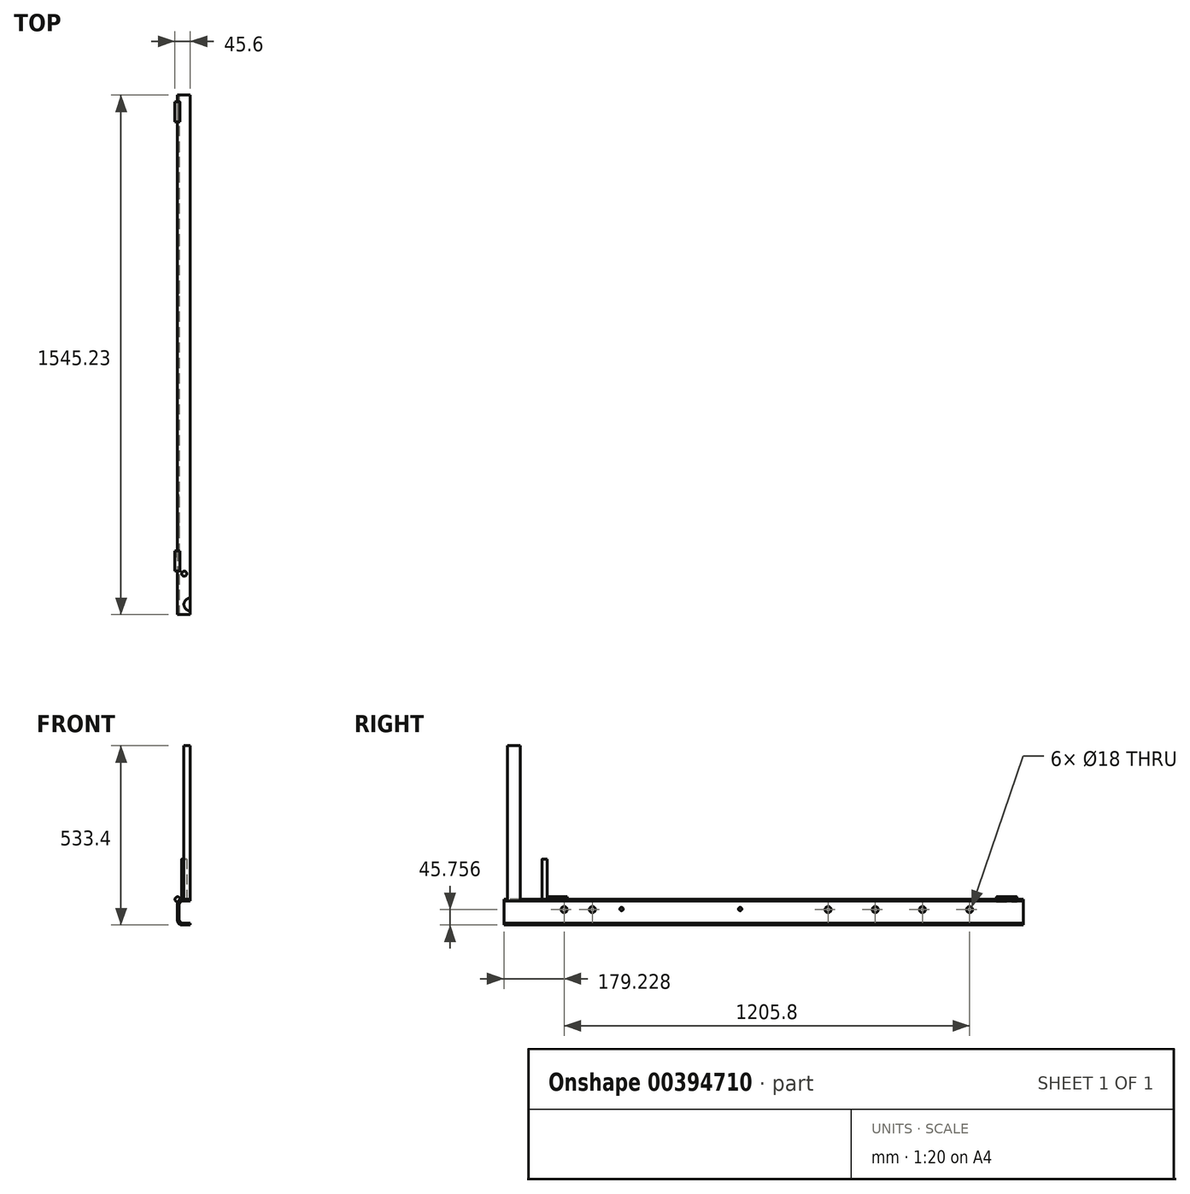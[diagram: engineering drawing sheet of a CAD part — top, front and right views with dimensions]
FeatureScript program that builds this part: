
annotation { "Feature Type Name" : "Feature", "Feature Type Description" : "" }
export const myFeature = defineFeature(function(context is Context, id is Id, definition is map)
    precondition{}
    {
        {
            var Q0;
            Q0=qCreatedBy(makeId("Front.planeOp"),FACE);
            var sketch = newSketch(context, id + "F0", { "sketchPlane" : qUnion([Q0])});
            skLineSegment(sketch, "E0.bottom", {"start": v(12.7, 0) * mm, "end": v(63.5, 0) * mm});
            skLineSegment(sketch, "E0.top", {"start": v(12.7, 76.2) * mm, "end": v(63.5, 76.2) * mm});
            skLineSegment(sketch, "E0.left", {"start": v(0, 12.7) * mm, "end": v(0, 63.5) * mm});
            skLineSegment(sketch, "E0.right", {"start": v(76.2, 12.7) * mm, "end": v(76.2, 63.5) * mm});
            skPoint(sketch, "E1.visualSharp", {"position": v(0, 76.2) * mm});
            skArc(sketch, "E1.filletArc", {"start": v(12.7, 76.2) * mm, "mid": v(3.72, 72.48) * mm, "end": v(0, 63.5) * mm});
            skPoint(sketch, "E2.visualSharp", {"position": v(76.2, 76.2) * mm});
            skArc(sketch, "E2.filletArc", {"start": v(76.2, 63.5) * mm, "mid": v(72.48, 72.48) * mm, "end": v(63.5, 76.2) * mm});
            skPoint(sketch, "E3.visualSharp", {"position": v(0, 0) * mm});
            skArc(sketch, "E3.filletArc", {"start": v(0, 12.7) * mm, "mid": v(3.72, 3.72) * mm, "end": v(12.7, 0) * mm});
            skPoint(sketch, "E4.visualSharp", {"position": v(76.2, 0) * mm});
            skArc(sketch, "E4.filletArc", {"start": v(63.5, 0) * mm, "mid": v(72.48, 3.72) * mm, "end": v(76.2, 12.7) * mm});
            skSolve(sketch);
        }
        {
            var Q0;
            Q0=qSketchRegion(id+"F0",true);
            extrude(context, id + "F1", {"entities" : qUnion([Q0]), "oppositeDirection" : true, "depth" : 1525.23 * mm});
        }
        {
            var Q0;
            Q0=makeQuery(id+"F1.opExtrude","CAP_FACE",FACE,{"disambiguationData":[OSD([sQuery(id+"F0.wireOp",EDGE,"E0.bottom"),sQuery(id+"F0.wireOp",EDGE,"E0.top"),sQuery(id+"F0.wireOp",EDGE,"E0.left"),sQuery(id+"F0.wireOp",EDGE,"E0.right"),sQuery(id+"F0.wireOp",EDGE,"E1.filletArc"),sQuery(id+"F0.wireOp",EDGE,"E2.filletArc"),sQuery(id+"F0.wireOp",EDGE,"E3.filletArc"),sQuery(id+"F0.wireOp",EDGE,"E4.filletArc")])],"isStart":true});
            var sketch = newSketch(context, id + "F2", { "sketchPlane" : qUnion([Q0])});
            skLineSegment(sketch, "E5", {"start": v(0, 38.1) * mm, "end": v(4.76, 38.1) * mm, "construction": true});
            skLineSegment(sketch, "E6", {"start": v(76.2, 38.1) * mm, "end": v(71.44, 38.1) * mm, "construction": true});
            skPoint(sketch, "E6.endSnap0", {"position": v(76.2, 38.1) * mm});
            skLineSegment(sketch, "E7", {"start": v(38.1, 76.2) * mm, "end": v(38.1, 71.44) * mm, "construction": true});
            skLineSegment(sketch, "E8", {"start": v(38.1, 0) * mm, "end": v(38.1, 4.76) * mm, "construction": true});
            skLineSegment(sketch, "E9", {"start": v(38.1, 4.76) * mm, "end": v(17.46, 4.76) * mm});
            skLineSegment(sketch, "E10", {"start": v(4.76, 17.46) * mm, "end": v(4.76, 58.74) * mm});
            skLineSegment(sketch, "E11", {"start": v(17.46, 71.44) * mm, "end": v(58.74, 71.44) * mm});
            skLineSegment(sketch, "E12", {"start": v(71.44, 58.74) * mm, "end": v(71.44, 17.46) * mm});
            skLineSegment(sketch, "E13", {"start": v(58.74, 4.76) * mm, "end": v(38.1, 4.76) * mm});
            skPoint(sketch, "E14.visualSharp", {"position": v(4.76, 71.44) * mm});
            skArc(sketch, "E14.filletArc", {"start": v(17.46, 71.44) * mm, "mid": v(8.48, 67.72) * mm, "end": v(4.76, 58.74) * mm});
            skPoint(sketch, "E15.visualSharp", {"position": v(71.44, 71.44) * mm});
            skArc(sketch, "E15.filletArc", {"start": v(71.44, 58.74) * mm, "mid": v(67.72, 67.72) * mm, "end": v(58.74, 71.44) * mm});
            skPoint(sketch, "E16.visualSharp", {"position": v(71.44, 4.76) * mm});
            skArc(sketch, "E16.filletArc", {"start": v(58.74, 4.76) * mm, "mid": v(67.72, 8.48) * mm, "end": v(71.44, 17.46) * mm});
            skPoint(sketch, "E17.visualSharp", {"position": v(4.76, 4.76) * mm});
            skArc(sketch, "E17.filletArc", {"start": v(4.76, 17.46) * mm, "mid": v(8.48, 8.48) * mm, "end": v(17.46, 4.76) * mm});
            skSolve(sketch);
        }
        {
            var Q0;
            Q0=makeQuery(id+"F2.imprint","IMPRINT",FACE,{"disambiguationData":[TD([[makeQuery(id+"F2.imprint","IMPRINT",EDGE,{"derivedFrom":sQuery(id+"F2.wireOp",EDGE,"E9")}),-1.0]])]});
            extrude(context, id + "F3", {"entities" : qUnion([Q0]), "operationType" : NewBodyOperationType.REMOVE, "oppositeDirection" : true, "depth" : 1525.23 * mm});
        }
        {
            var Q0;
            Q0=makeQuery(id+"F1.opExtrude","SWEPT_FACE",FACE,{"disambiguationData":[OSD([sQuery(id+"F0.wireOp",EDGE,"E0.right")])]});
            var sketch = newSketch(context, id + "F4", { "sketchPlane" : qUnion([Q0])});
            skLineSegment(sketch, "E18", {"start": v(1525.23, 63.5) * mm, "end": v(1525.23, 76.2) * mm, "construction": true});
            skLineSegment(sketch, "E19", {"start": v(1525.23, 76.2) * mm, "end": v(1525.23, 46.2) * mm, "construction": true});
            skLineSegment(sketch, "E20", {"start": v(1525.23, 46.2) * mm, "end": v(1335.23, 46.2) * mm, "construction": true});
            skLineSegment(sketch, "E21", {"start": v(1335.23, 46.2) * mm, "end": v(1105.03, 46.2) * mm, "construction": true});
            skLineSegment(sketch, "E22", {"start": v(1105.03, 46.2) * mm, "end": v(653.53, 46.2) * mm, "construction": true});
            skLineSegment(sketch, "E23", {"start": v(653.53, 46.2) * mm, "end": v(381.53, 46.2) * mm, "construction": true});
            skLineSegment(sketch, "E24", {"start": v(381.53, 46.2) * mm, "end": v(179.53, 46.2) * mm, "construction": true});
            skSolve(sketch);
        }
        {
            var Q0;
            Q0=sQuery(id+"F4.wireOp",VERTEX,"E21.start");
            var Q1;
            Q1=sQuery(id+"F4.wireOp",VERTEX,"E21.end");
            var Q2;
            Q2=sQuery(id+"F4.wireOp",VERTEX,"E23.start");
            var Q3;
            Q3=sQuery(id+"F4.wireOp",VERTEX,"E24.start");
            var Q4;
            Q4=sQuery(id+"F4.wireOp",VERTEX,"15NCYrLK-5f7F-d4hg-Meu1-zmrvhpbFYJVG.start");
            var Q5;
            Q5=sQuery(id+"F4.wireOp",VERTEX,"E24.end");
            var Q6;
            Q6=makeQuery(id+"F1.opExtrude","SWEPT_BODY",BODY,{"disambiguationData":[OSD([sQuery(id+"F0.wireOp",EDGE,"E0.bottom"),sQuery(id+"F0.wireOp",EDGE,"E0.top"),sQuery(id+"F0.wireOp",EDGE,"E0.left"),sQuery(id+"F0.wireOp",EDGE,"E0.right"),sQuery(id+"F0.wireOp",EDGE,"E1.filletArc"),sQuery(id+"F0.wireOp",EDGE,"E2.filletArc"),sQuery(id+"F0.wireOp",EDGE,"E3.filletArc"),sQuery(id+"F0.wireOp",EDGE,"E4.filletArc")])]});
            hole(context, id + "F5", {"style" : HoleStyle.SIMPLE, "endStyle" : HoleEndStyle.BLIND, "holeDiameter" : 19 * mm, "holeDepth" : 5 * mm, "isTappedThrough" : true, "tappedDepth" : 12 * mm, "tapClearance" : 3, "locations" : qUnion([Q0, Q1, Q2, Q3, Q4, Q5]), "scope" : qUnion([Q6])});
        }
        {
            var Q0;
            Q0=makeQuery(id+"F1.opExtrude","SWEPT_FACE",FACE,{"disambiguationData":[OSD([sQuery(id+"F0.wireOp",EDGE,"E0.right")])]});
            var sketch = newSketch(context, id + "F6", { "sketchPlane" : qUnion([Q0])});
            skLineSegment(sketch, "E25", {"start": v(1525.23, 63.5) * mm, "end": v(1525.23, 76.2) * mm});
            skLineSegment(sketch, "E26", {"start": v(1525.23, 76.2) * mm, "end": v(1525.23, 31.2) * mm, "construction": true});
            skLineSegment(sketch, "E27", {"start": v(1525.23, 31.2) * mm, "end": v(1442.06, 31.2) * mm, "construction": true});
            skLineSegment(sketch, "E28", {"start": v(1442.06, 31.2) * mm, "end": v(1218.7, 31.2) * mm, "construction": true});
            skLineSegment(sketch, "E29", {"start": v(1218.7, 31.2) * mm, "end": v(979.53, 31.2) * mm, "construction": true});
            skLineSegment(sketch, "E30", {"start": v(979.53, 31.2) * mm, "end": v(760.33, 31.2) * mm, "construction": true});
            skLineSegment(sketch, "E31", {"start": v(760.33, 31.2) * mm, "end": v(501.13, 31.2) * mm, "construction": true});
            skLineSegment(sketch, "E32", {"start": v(501.13, 31.2) * mm, "end": v(261.93, 31.2) * mm, "construction": true});
            skSolve(sketch);
        }
        {
            var Q0;
            Q0=sQuery(id+"F6.wireOp",VERTEX,"E32.end");
            var Q1;
            Q1=sQuery(id+"F6.wireOp",VERTEX,"E32.start");
            var Q2;
            Q2=sQuery(id+"F6.wireOp",VERTEX,"E31.start");
            var Q3;
            Q3=sQuery(id+"F6.wireOp",VERTEX,"E30.start");
            var Q4;
            Q4=sQuery(id+"F6.wireOp",VERTEX,"E28.end");
            var Q5;
            Q5=makeQuery(id+"F1.opExtrude","SWEPT_BODY",BODY,{"disambiguationData":[OSD([sQuery(id+"F0.wireOp",EDGE,"E0.bottom"),sQuery(id+"F0.wireOp",EDGE,"E0.top"),sQuery(id+"F0.wireOp",EDGE,"E0.left"),sQuery(id+"F0.wireOp",EDGE,"E0.right"),sQuery(id+"F0.wireOp",EDGE,"E1.filletArc"),sQuery(id+"F0.wireOp",EDGE,"E2.filletArc"),sQuery(id+"F0.wireOp",EDGE,"E3.filletArc"),sQuery(id+"F0.wireOp",EDGE,"E4.filletArc")])]});
            hole(context, id + "F7", {"style" : HoleStyle.SIMPLE, "endStyle" : HoleEndStyle.BLIND, "holeDiameter" : 9 * mm, "holeDepth" : 5 * mm, "isTappedThrough" : true, "tappedDepth" : 12 * mm, "tapClearance" : 3, "locations" : qUnion([Q0, Q1, Q2, Q3, Q4]), "scope" : qUnion([Q5])});
        }
        {
            var Q0;
            Q0=makeQuery(id+"F1.opExtrude","SWEPT_FACE",FACE,{"disambiguationData":[OSD([sQuery(id+"F0.wireOp",EDGE,"E0.top")])]});
            var sketch = newSketch(context, id + "F8", { "sketchPlane" : qUnion([Q0])});
            skLineSegment(sketch, "E33", {"start": v(38.1, 0) * mm, "end": v(38.1, 30) * mm, "construction": true});
            skCircle(sketch, "E34", {"center": v(38.1, 30) * mm, "radius": 19.05 * mm});
            skSolve(sketch);
        }
        {
            var Q0;
            Q0=makeQuery(id+"F8.imprint","IMPRINT",FACE,{"disambiguationData":[TD([[makeQuery(id+"F8.imprint","IMPRINT",EDGE,{"derivedFrom":sQuery(id+"F8.wireOp",EDGE,"E34")}),1.0]])]});
            extrude(context, id + "F9", {"entities" : qUnion([Q0]), "operationType" : NewBodyOperationType.ADD, "depth" : 457.2 * mm});
        }
        {
            var Q0;
            {var subQ0=sQuery(id+"F0.wireOp",EDGE,"E0.top");Q0=makeQuery(id+"FTddWvQlXHfw4Uw_1.boolean.opBoolean","MERGE",FACE,{"derivedFrom":[makeQuery(id+"F1.opExtrude","SWEPT_FACE",FACE,{"disambiguationData":[OSD([subQ0])]}),makeQuery(id+"FTddWvQlXHfw4Uw_1.opExtrude","SWEPT_FACE",FACE,{"disambiguationData":[OSD([subQ0])]})]});}
            var sketch = newSketch(context, id + "F10", { "sketchPlane" : qUnion([Q0])});
            skLineSegment(sketch, "E35", {"start": v(12.7, 0) * mm, "end": v(12.7, 30) * mm, "construction": true});
            skLineSegment(sketch, "E36", {"start": v(12.7, 30) * mm, "end": v(12.7, 49.05) * mm, "construction": true});
            skLineSegment(sketch, "E37", {"start": v(12.7, 49.05) * mm, "end": v(12.7, 121.55) * mm, "construction": true});
            skLineSegment(sketch, "E38", {"start": v(12.7, 121.55) * mm, "end": v(20.2, 121.55) * mm, "construction": true});
            skCircle(sketch, "E39", {"center": v(20.2, 121.55) * mm, "radius": 7.5 * mm});
            skSolve(sketch);
        }
        {
            var Q0;
            Q0=makeQuery(id+"F10.imprint","IMPRINT",FACE,{"disambiguationData":[TD([[makeQuery(id+"F10.imprint","IMPRINT",EDGE,{"derivedFrom":sQuery(id+"F10.wireOp",EDGE,"E39")}),1.0]])]});
            extrude(context, id + "F11", {"entities" : qUnion([Q0]), "operationType" : NewBodyOperationType.ADD, "depth" : 120 * mm});
        }
        {
            var Q0;
            Q0=makeQuery(id+"F1.opExtrude","CAP_FACE",FACE,{"disambiguationData":[OSD([sQuery(id+"F0.wireOp",EDGE,"E0.bottom"),sQuery(id+"F0.wireOp",EDGE,"E0.top"),sQuery(id+"F0.wireOp",EDGE,"E0.left"),sQuery(id+"F0.wireOp",EDGE,"E0.right"),sQuery(id+"F0.wireOp",EDGE,"E1.filletArc"),sQuery(id+"F0.wireOp",EDGE,"E2.filletArc"),sQuery(id+"F0.wireOp",EDGE,"E3.filletArc"),sQuery(id+"F0.wireOp",EDGE,"E4.filletArc")])],"isStart":false});
            extrude(context, id + "F12", {"entities" : qUnion([Q0]), "operationType" : NewBodyOperationType.ADD, "depth" : 20 * mm});
        }
        {
            var Q0;
            {var subQ0=sQuery(id+"F0.wireOp",EDGE,"E0.top");Q0=makeQuery(id+"F12.boolean.opBoolean","MERGE",FACE,{"derivedFrom":[makeQuery(id+"F1.opExtrude","SWEPT_FACE",FACE,{"disambiguationData":[OSD([subQ0])]}),makeQuery(id+"F12.opExtrude","SWEPT_FACE",FACE,{"disambiguationData":[OSD([subQ0])]})]});}
            var sketch = newSketch(context, id + "F13", { "sketchPlane" : qUnion([Q0])});
            skLineSegment(sketch, "E40", {"start": v(12.7, 121.55) * mm, "end": v(20.2, 121.55) * mm, "construction": true});
            skLineSegment(sketch, "E41", {"start": v(20.2, 121.55) * mm, "end": v(20.2, 129.05) * mm, "construction": true});
            skLineSegment(sketch, "E42", {"start": v(20.2, 129.05) * mm, "end": v(55.2, 129.05) * mm, "construction": true});
            skLineSegment(sketch, "E43", {"start": v(55.2, 129.05) * mm, "end": v(55.2, 0) * mm, "construction": true});
            skSolve(sketch);
        }
        {
            var Q0;
            {var subQ0=sQuery(id+"F0.wireOp",EDGE,"E0.right");Q0=makeQuery(id+"F12.boolean.opBoolean","MERGE",FACE,{"derivedFrom":[makeQuery(id+"F1.opExtrude","SWEPT_FACE",FACE,{"disambiguationData":[OSD([subQ0])]}),makeQuery(id+"F12.opExtrude","SWEPT_FACE",FACE,{"disambiguationData":[OSD([subQ0])]})]});}
            var sketch = newSketch(context, id + "F14", { "sketchPlane" : qUnion([Q0])});
            skLineSegment(sketch, "E44", {"start": v(0, 63.5) * mm, "end": v(129.05, 63.5) * mm, "construction": true});
            skSolve(sketch);
        }
        {
            var Q0;
            Q0=sQuery(id+"F13.wireOp",VERTEX,"E41.end");
            var Q1;
            Q1=sQuery(id+"F13.wireOp",VERTEX,"E42.end");
            var Q2;
            Q2=sQuery(id+"F14.wireOp",VERTEX,"E44.end");
            cPlane(context, id + "F15", {"entities" : qUnion([Q0, Q1, Q2]), "cplaneType" : CPlaneType.THREE_POINT, "offset" : 25 * mm, "width" : 150 * mm, "height" : 150 * mm});
        }
        {
            var Q0;
            Q0=qCreatedBy(id+"F15.planeOp",FACE);
            var sketch = newSketch(context, id + "F16", { "sketchPlane" : qUnion([Q0])});
            skLineSegment(sketch, "E45", {"start": v(0, 0) * mm, "end": v(0, 76.2) * mm, "construction": true});
            skCircle(sketch, "E46", {"center": v(0, 76.2) * mm, "radius": 7.5 * mm});
            skSolve(sketch);
        }
        {
            var Q0;
            Q0=qSketchRegion(id+"F16",true);
            extrude(context, id + "F17", {"entities" : qUnion([Q0]), "operationType" : NewBodyOperationType.ADD, "oppositeDirection" : true, "depth" : 60 * mm});
        }
        {
            var Q0;
            {var subQ6=sQuery(id+"F0.wireOp",EDGE,"E0.top");Q0=makeQuery(id+"F13.imprint","IMPRINT",FACE,{"disambiguationData":[TD([[makeQuery(id+"F13.imprint","IMPRINT",EDGE,{"derivedFrom":makeQuery(id+"F1.opExtrude","CAP_EDGE",EDGE,{"disambiguationData":[OSD([subQ6])],"isStart":true})}),1.0]])]});}
            var sketch = newSketch(context, id + "F18", { "sketchPlane" : qUnion([Q0])});
            skLineSegment(sketch, "E47", {"start": v(0, 0) * mm, "end": v(38.1, 0) * mm, "construction": true});
            skLineSegment(sketch, "E48", {"start": v(38.1, 0) * mm, "end": v(38.1, 1545.43) * mm, "construction": true});
            skSolve(sketch);
        }
        {
            var Q0;
            {var subQ6=sQuery(id+"F0.wireOp",EDGE,"E0.top");Q0=makeQuery(id+"F13.imprint","IMPRINT",FACE,{"disambiguationData":[TD([[makeQuery(id+"F13.imprint","IMPRINT",EDGE,{"derivedFrom":makeQuery(id+"F1.opExtrude","CAP_EDGE",EDGE,{"disambiguationData":[OSD([subQ6])],"isStart":true})}),1.0]])]});}
            var sketch = newSketch(context, id + "F19", { "sketchPlane" : qUnion([Q0])});
            skLineSegment(sketch, "E49", {"start": v(0, 0) * mm, "end": v(0, 1525.23) * mm, "construction": true});
            skLineSegment(sketch, "E50", {"start": v(0, 1525.23) * mm, "end": v(75.73, 1525.23) * mm, "construction": true});
            skSolve(sketch);
        }
        {
            var Q0;
            {var subQ0=sQuery(id+"F0.wireOp",EDGE,"E0.right");Q0=makeQuery(id+"F14.imprint","IMPRINT",FACE,{"disambiguationData":[TD([[makeQuery(id+"F14.imprint","IMPRINT",EDGE,{"derivedFrom":makeQuery(id+"F1.opExtrude","CAP_EDGE",EDGE,{"disambiguationData":[OSD([subQ0])],"isStart":true})}),-1.0]])]});}
            var sketch = newSketch(context, id + "F20", { "sketchPlane" : qUnion([Q0])});
            skLineSegment(sketch, "E51", {"start": v(0, 33.48) * mm, "end": v(1525.23, 33.48) * mm, "construction": true});
            skSolve(sketch);
        }
        {
            var Q0;
            Q0=sQuery(id+"F20.wireOp",VERTEX,"E51.end");
            var Q1;
            Q1=sQuery(id+"F19.wireOp",VERTEX,"E50.end");
            var Q2;
            Q2=sQuery(id+"F19.wireOp",VERTEX,"E49.end");
            cPlane(context, id + "F21", {"entities" : qUnion([Q0, Q1, Q2]), "cplaneType" : CPlaneType.THREE_POINT, "offset" : 25 * mm, "width" : 150 * mm, "height" : 150 * mm});
        }
        {
            var Q0;
            Q0=qCreatedBy(id+"F21.planeOp",FACE);
            var sketch = newSketch(context, id + "F22", { "sketchPlane" : qUnion([Q0])});
            skLineSegment(sketch, "E52", {"start": v(0, 0) * mm, "end": v(0, 76.2) * mm, "construction": true});
            skCircle(sketch, "E53", {"center": v(0, 76.2) * mm, "radius": 7.5 * mm});
            skSolve(sketch);
        }
        {
            var Q0;
            Q0=makeQuery(id+"F22.imprint","IMPRINT",FACE,{"disambiguationData":[TD([[makeQuery(id+"F22.imprint","IMPRINT",EDGE,{"derivedFrom":sQuery(id+"F22.wireOp",EDGE,"E53")}),1.0]])]});
            extrude(context, id + "F23", {"entities" : qUnion([Q0]), "operationType" : NewBodyOperationType.ADD, "oppositeDirection" : true, "depth" : 60 * mm});
        }
        {
            var Q0;
            Q0=makeQuery(id+"F12.opExtrude","CAP_EDGE",EDGE,{"disambiguationData":[OSD([sQuery(id+"F0.wireOp",EDGE,"E0.top")])],"isStart":false});
            cPoint(context, id + "F24", {"entities" : qUnion([Q0]), "parameter" : 0.5});
        }
        {
            var Q0;
            Q0=sQuery(id+"F18.wireOp",EDGE,"E48");
            cPoint(context, id + "F25", {"entities" : qUnion([Q0]), "parameter" : 0.5});
        }
        {
            var Q0;
            Q0=makeQuery(id+"F12.opExtrude","CAP_EDGE",EDGE,{"disambiguationData":[OSD([sQuery(id+"F0.wireOp",EDGE,"E0.bottom")])],"isStart":false});
            cPoint(context, id + "F26", {"entities" : qUnion([Q0]), "parameter" : 0.5});
        }
        {
            var Q0;
            Q0=qCreatedBy(id+"F24",VERTEX);
            var Q1;
            Q1=qCreatedBy(id+"F25",VERTEX);
            var Q2;
            Q2=qCreatedBy(id+"F26",VERTEX);
            cPlane(context, id + "F27", {"entities" : qUnion([Q0, Q1, Q2]), "cplaneType" : CPlaneType.THREE_POINT, "offset" : 25 * mm, "width" : 150 * mm, "height" : 150 * mm});
        }
        {
            var Q0;
            Q0=sQuery(id+"F6.wireOp",VERTEX,"E28.start");
            var Q1;
            Q1=makeQuery(id+"F1.opExtrude","SWEPT_BODY",BODY,{"disambiguationData":[OSD([sQuery(id+"F0.wireOp",EDGE,"E0.bottom"),sQuery(id+"F0.wireOp",EDGE,"E0.top"),sQuery(id+"F0.wireOp",EDGE,"E0.left"),sQuery(id+"F0.wireOp",EDGE,"E0.right"),sQuery(id+"F0.wireOp",EDGE,"E1.filletArc"),sQuery(id+"F0.wireOp",EDGE,"E2.filletArc"),sQuery(id+"F0.wireOp",EDGE,"E3.filletArc"),sQuery(id+"F0.wireOp",EDGE,"E4.filletArc")])]});
            hole(context, id + "F28", {"style" : HoleStyle.SIMPLE, "endStyle" : HoleEndStyle.BLIND, "holeDiameter" : 15 * mm, "holeDepth" : 5 * mm, "isTappedThrough" : true, "tappedDepth" : 12 * mm, "tapClearance" : 3, "locations" : qUnion([Q0]), "scope" : qUnion([Q1])});
        }
        {
            var Q0;
            {var subQ0=sQuery(id+"F0.wireOp",EDGE,"E0.left");Q0=makeQuery(id+"F12.boolean.opBoolean","MERGE",FACE,{"derivedFrom":[makeQuery(id+"F1.opExtrude","SWEPT_FACE",FACE,{"disambiguationData":[OSD([subQ0])]}),makeQuery(id+"F12.opExtrude","SWEPT_FACE",FACE,{"disambiguationData":[OSD([subQ0])]})]});}
            var sketch = newSketch(context, id + "F29", { "sketchPlane" : qUnion([Q0])});
            skLineSegment(sketch, "E54", {"start": v(0, 38.1) * mm, "end": v(0, 30.76) * mm, "construction": true});
            skLineSegment(sketch, "E55", {"start": v(0, 30.76) * mm, "end": v(0, 45.76) * mm, "construction": true});
            skLineSegment(sketch, "E56", {"start": v(-179.23, 45.76) * mm, "end": v(-263.44, 45.76) * mm, "construction": true});
            skLineSegment(sketch, "E57", {"start": v(-263.44, 45.76) * mm, "end": v(-964.43, 45.76) * mm, "construction": true});
            skLineSegment(sketch, "E58", {"start": v(-964.43, 45.76) * mm, "end": v(-1104.63, 45.76) * mm, "construction": true});
            skLineSegment(sketch, "E59", {"start": v(-1104.63, 45.76) * mm, "end": v(-1244.83, 45.76) * mm, "construction": true});
            skLineSegment(sketch, "E60", {"start": v(-1244.83, 45.76) * mm, "end": v(-1385.03, 45.76) * mm, "construction": true});
            skLineSegment(sketch, "E61", {"start": v(-1385.03, 45.76) * mm, "end": v(-1545.23, 45.76) * mm});
            skSolve(sketch);
        }
        {
            var Q0;
            Q0=sQuery(id+"F29.wireOp",VERTEX,"E60.end");
            var Q1;
            Q1=sQuery(id+"F29.wireOp",VERTEX,"E59.end");
            var Q2;
            Q2=sQuery(id+"F29.wireOp",VERTEX,"E59.start");
            var Q3;
            Q3=sQuery(id+"F29.wireOp",VERTEX,"E58.start");
            var Q4;
            Q4=sQuery(id+"F29.wireOp",VERTEX,"E57.start");
            var Q5;
            Q5=sQuery(id+"F29.wireOp",VERTEX,"E56.start");
            var Q6;
            Q6=makeQuery(id+"F1.opExtrude","SWEPT_BODY",BODY,{"disambiguationData":[OSD([sQuery(id+"F0.wireOp",EDGE,"E0.bottom"),sQuery(id+"F0.wireOp",EDGE,"E0.top"),sQuery(id+"F0.wireOp",EDGE,"E0.left"),sQuery(id+"F0.wireOp",EDGE,"E0.right"),sQuery(id+"F0.wireOp",EDGE,"E1.filletArc"),sQuery(id+"F0.wireOp",EDGE,"E2.filletArc"),sQuery(id+"F0.wireOp",EDGE,"E3.filletArc"),sQuery(id+"F0.wireOp",EDGE,"E4.filletArc")])]});
            hole(context, id + "F30", {"style" : HoleStyle.SIMPLE, "endStyle" : HoleEndStyle.BLIND, "holeDiameter" : 18 * mm, "holeDepth" : 5 * mm, "isTappedThrough" : true, "tappedDepth" : 12 * mm, "tapClearance" : 3, "locations" : qUnion([Q0, Q1, Q2, Q3, Q4, Q5]), "scope" : qUnion([Q6])});
        }
        {
            var Q0;
            {var subQ0=sQuery(id+"F0.wireOp",EDGE,"E0.left");Q0=makeQuery(id+"F12.boolean.opBoolean","MERGE",FACE,{"derivedFrom":[makeQuery(id+"F1.opExtrude","SWEPT_FACE",FACE,{"disambiguationData":[OSD([subQ0])]}),makeQuery(id+"F12.opExtrude","SWEPT_FACE",FACE,{"disambiguationData":[OSD([subQ0])]})]});}
            var sketch = newSketch(context, id + "F31", { "sketchPlane" : qUnion([Q0])});
            skLineSegment(sketch, "E62", {"start": v(-1545.23, 38.1) * mm, "end": v(-1545.23, 32.4) * mm, "construction": true});
            skLineSegment(sketch, "E63", {"start": v(-1545.23, 32.4) * mm, "end": v(-1545.23, 47.4) * mm, "construction": true});
            skLineSegment(sketch, "E64", {"start": v(-1545.23, 47.4) * mm, "end": v(-702.73, 47.4) * mm, "construction": true});
            skLineSegment(sketch, "E65", {"start": v(-702.73, 47.4) * mm, "end": v(-350.23, 47.4) * mm, "construction": true});
            skSolve(sketch);
        }
        {
            var Q0;
            Q0=sQuery(id+"F31.wireOp",VERTEX,"E65.start");
            var Q1;
            Q1=sQuery(id+"F31.wireOp",VERTEX,"E65.end");
            var Q2;
            Q2=makeQuery(id+"F1.opExtrude","SWEPT_BODY",BODY,{"disambiguationData":[OSD([sQuery(id+"F0.wireOp",EDGE,"E0.bottom"),sQuery(id+"F0.wireOp",EDGE,"E0.top"),sQuery(id+"F0.wireOp",EDGE,"E0.left"),sQuery(id+"F0.wireOp",EDGE,"E0.right"),sQuery(id+"F0.wireOp",EDGE,"E1.filletArc"),sQuery(id+"F0.wireOp",EDGE,"E2.filletArc"),sQuery(id+"F0.wireOp",EDGE,"E3.filletArc"),sQuery(id+"F0.wireOp",EDGE,"E4.filletArc")])]});
            hole(context, id + "F32", {"style" : HoleStyle.SIMPLE, "endStyle" : HoleEndStyle.BLIND, "holeDiameter" : 10 * mm, "holeDepth" : 5 * mm, "isTappedThrough" : true, "tappedDepth" : 12 * mm, "tapClearance" : 3, "locations" : qUnion([Q0, Q1]), "scope" : qUnion([Q2])});
        }
        {
            var Q0;
            {var subQ0=sQuery(id+"F0.wireOp",EDGE,"E0.bottom");Q0=makeQuery(id+"F12.boolean.opBoolean","MERGE",FACE,{"derivedFrom":[makeQuery(id+"F1.opExtrude","SWEPT_FACE",FACE,{"disambiguationData":[OSD([subQ0])]}),makeQuery(id+"F12.opExtrude","SWEPT_FACE",FACE,{"disambiguationData":[OSD([subQ0])]})]});}
            var sketch = newSketch(context, id + "F33", { "sketchPlane" : qUnion([Q0])});
            skLineSegment(sketch, "E66.bottom", {"start": v(38.1, 0) * mm, "end": v(113.1, 0) * mm});
            skLineSegment(sketch, "E66.top", {"start": v(38.1, -1545.23) * mm, "end": v(113.1, -1545.23) * mm});
            skLineSegment(sketch, "E66.left", {"start": v(38.1, 0) * mm, "end": v(38.1, -1545.23) * mm});
            skLineSegment(sketch, "E66.right", {"start": v(113.1, 0) * mm, "end": v(113.1, -1545.23) * mm});
            skSolve(sketch);
        }
        {
            var Q0;
            Q0 = qSketchRegion(id + "F33", true);
            extrude(context, id + "F34", {"entities" : qUnion([Q0]), "operationType" : NewBodyOperationType.REMOVE, "oppositeDirection" : true, "depth" : 2500 * mm});
        }
    });
